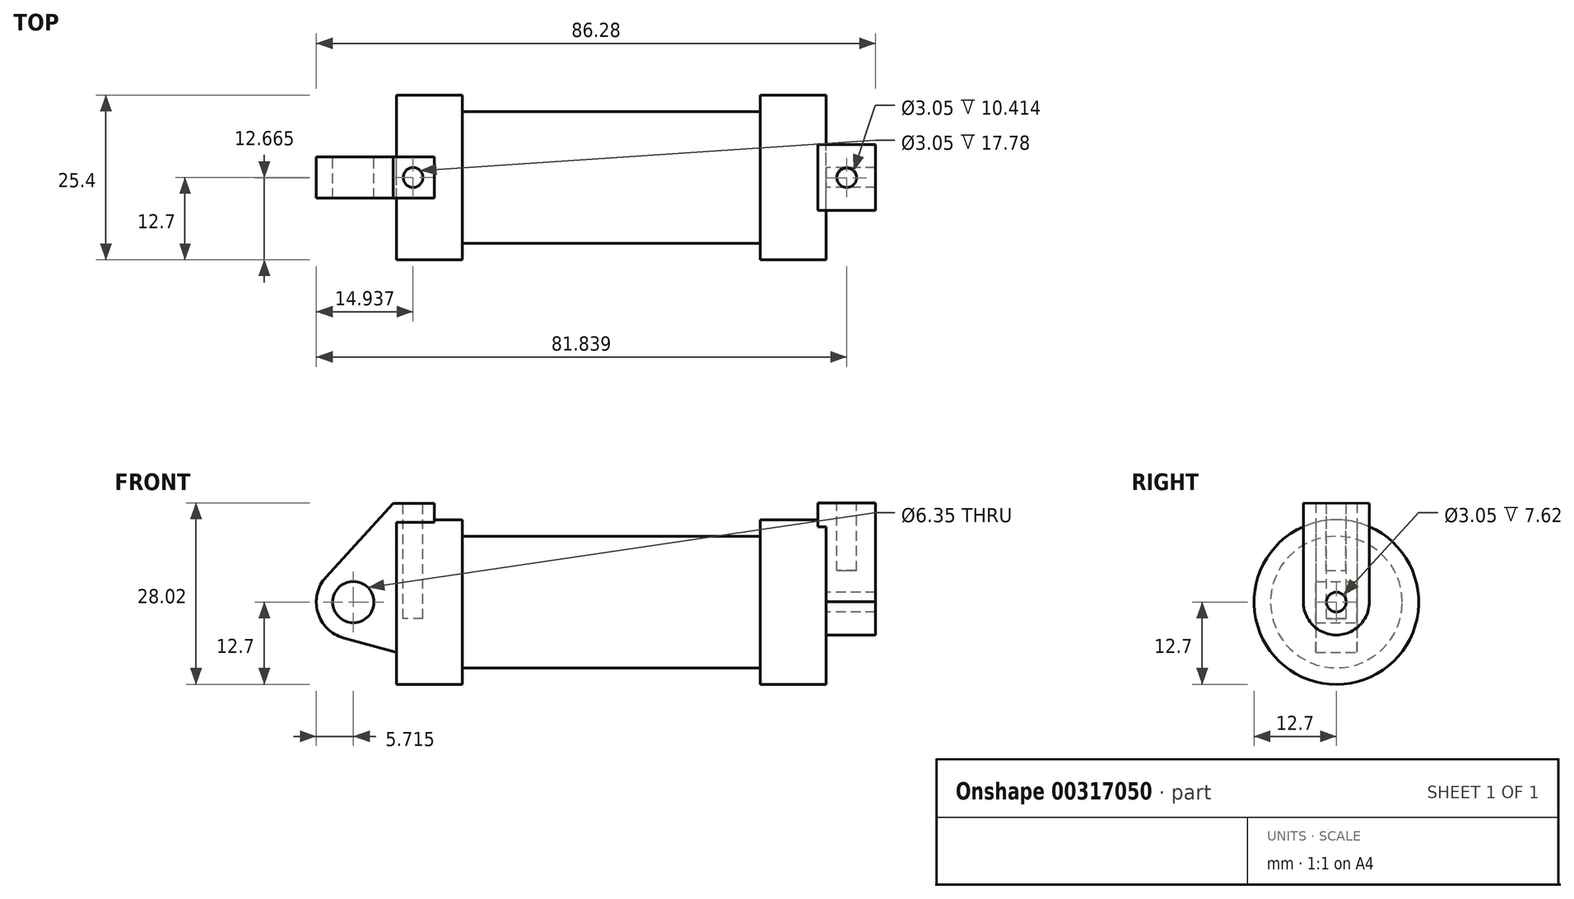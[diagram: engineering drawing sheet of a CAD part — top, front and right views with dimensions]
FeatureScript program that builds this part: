
annotation { "Feature Type Name" : "Feature", "Feature Type Description" : "" }
export const myFeature = defineFeature(function(context is Context, id is Id, definition is map)
    precondition{}
    {
        {
            var Q0;
            Q0=qCreatedBy(makeId("Front.planeOp"),FACE);
            var sketch = newSketch(context, id + "F0", { "sketchPlane" : qUnion([Q0])});
            skLineSegment(sketch, "E0", {"start": v(0, 0) * mm, "end": v(0, 12.7) * mm});
            skLineSegment(sketch, "E1", {"start": v(0, 12.7) * mm, "end": v(10.16, 12.7) * mm});
            skLineSegment(sketch, "E2", {"start": v(10.16, 12.7) * mm, "end": v(10.16, 10.16) * mm});
            skLineSegment(sketch, "E3", {"start": v(10.16, 10.16) * mm, "end": v(56.13, 10.16) * mm});
            skLineSegment(sketch, "E4", {"start": v(56.13, 10.16) * mm, "end": v(56.13, 12.7) * mm});
            skLineSegment(sketch, "E5", {"start": v(56.13, 12.7) * mm, "end": v(66.3, 12.7) * mm});
            skLineSegment(sketch, "E6", {"start": v(66.3, 12.7) * mm, "end": v(66.3, 0) * mm});
            skLineSegment(sketch, "E7", {"start": v(66.3, 0) * mm, "end": v(0, 0) * mm});
            skLineSegment(sketch, "E8", {"start": v(5.84, 15.24) * mm, "end": v(-0.5, 15.24) * mm});
            skLineSegment(sketch, "E9", {"start": v(-0.5, 15.24) * mm, "end": v(-10.88, 3.85) * mm});
            skLineSegment(sketch, "E10", {"start": v(0, 0) * mm, "end": v(-6.65, 0) * mm});
            skCircle(sketch, "E11", {"center": v(-6.65, 0) * mm, "radius": 5.72 * mm});
            skCircle(sketch, "E12", {"center": v(-6.65, 0) * mm, "radius": 3.18 * mm});
            skLineSegment(sketch, "E13", {"start": v(5.84, 15.24) * mm, "end": v(5.84, -9.4) * mm});
            skLineSegment(sketch, "E14", {"start": v(5.84, -9.4) * mm, "end": v(-8.18, -5.5) * mm});
            skSolve(sketch);
        }
        {
            var Q0;
            {var subQ0=sQuery(id+"F0.wireOp",EDGE,"E2");Q0=makeQuery(id+"F0.imprint","IMPRINT",FACE,{"disambiguationData":[TD([[makeQuery(id+"F0.imprint","IMPRINT",EDGE,{"derivedFrom":subQ0}),-1.0]])]});}
            var Q1;
            {var subQ0=sQuery(id+"F0.wireOp",EDGE,"E0");Q1=makeQuery(id+"F0.imprint","IMPRINT",FACE,{"disambiguationData":[TD([[makeQuery(id+"F0.imprint","IMPRINT",EDGE,{"derivedFrom":subQ0}),-1.0]])]});}
            var Q2;
            Q2=sQuery(id+"F0.wireOp",EDGE,"E7");
            revolve(context, id + "F1", {"entities" : qUnion([Q0, Q1]), "axis" : qUnion([Q2]), "revolveType" : RevolveType.FULL});
        }
        {
            var Q0;
            {var subQ1=sQuery(id+"F0.wireOp",EDGE,"E0");Q0=makeQuery(id+"F0.imprint","IMPRINT",FACE,{"disambiguationData":[TD([[makeQuery(id+"F0.imprint","IMPRINT",EDGE,{"derivedFrom":subQ1}),1.0]])]});}
            var Q1;
            {var subQ5=sQuery(id+"F0.wireOp",EDGE,"E12");Q1=makeQuery(id+"F0.imprint","IMPRINT",FACE,{"disambiguationData":[TD([[makeQuery(id+"F0.imprint","IMPRINT",EDGE,{"derivedFrom":subQ5}),-1.0]])]});}
            var Q2;
            {var subQ0=sQuery(id+"F0.wireOp",EDGE,"E14");Q2=makeQuery(id+"F0.imprint","IMPRINT",FACE,{"disambiguationData":[TD([[makeQuery(id+"F0.imprint","IMPRINT",EDGE,{"derivedFrom":subQ0}),-1.0]])]});}
            var Q3;
            {var subQ0=sQuery(id+"F0.wireOp",EDGE,"E0");Q3=makeQuery(id+"F0.imprint","IMPRINT",FACE,{"disambiguationData":[TD([[makeQuery(id+"F0.imprint","IMPRINT",EDGE,{"derivedFrom":subQ0}),-1.0]])]});}
            extrude(context, id + "F2", {"entities" : qUnion([Q0, Q1, Q2, Q3]), "operationType" : NewBodyOperationType.ADD, "depth" : 3.17 * mm});
        }
        {
            var Q0;
            Q0=makeQuery(id+"F2.opExtrude","CAP_FACE",FACE,{"disambiguationData":[OSD([sQuery(id+"F0.wireOp",EDGE,"E8"),sQuery(id+"F0.wireOp",EDGE,"E9"),sQuery(id+"F0.wireOp",EDGE,"E11"),sQuery(id+"F0.wireOp",EDGE,"E12"),sQuery(id+"F0.wireOp",EDGE,"E13"),sQuery(id+"F0.wireOp",EDGE,"E14")])],"isStart":false});
            extrude(context, id + "F3", {"entities" : qUnion([Q0]), "operationType" : NewBodyOperationType.ADD, "oppositeDirection" : true, "depth" : 6.35 * mm});
        }
        {
            var Q0;
            Q0=makeQuery(id+"F1.opRevolve","SWEPT_FACE",FACE,{"disambiguationData":[OSD([sQuery(id+"F0.wireOp",EDGE,"E6")])]});
            var sketch = newSketch(context, id + "F4", { "sketchPlane" : qUnion([Q0])});
            skCircle(sketch, "E15", {"center": v(0, 0) * mm, "radius": 5.08 * mm});
            skCircle(sketch, "E16", {"center": v(0, 0) * mm, "radius": 1.52 * mm});
            skLineSegment(sketch, "E17", {"start": v(-5.08, 0.08) * mm, "end": v(-5.08, 15.32) * mm});
            skLineSegment(sketch, "E18", {"start": v(5.08, 0) * mm, "end": v(5.08, 15.25) * mm});
            skLineSegment(sketch, "E19", {"start": v(-5.08, 15.32) * mm, "end": v(5.08, 15.25) * mm});
            skSolve(sketch);
        }
        {
            var Q0;
            Q0=makeQuery(id+"F4.imprint","IMPRINT",FACE,{"disambiguationData":[TD([[makeQuery(id+"F4.imprint","IMPRINT",EDGE,{"derivedFrom":sQuery(id+"F4.wireOp",EDGE,"E16")}),-1.0]])]});
            var Q1;
            {var subQ0=sQuery(id+"F4.wireOp",EDGE,"E17");var subQ1=sQuery(id+"F4.wireOp",EDGE,"E15");var subQ2=makeQuery(id+"F4.imprint","INTERSECT",VERTEX,{"derivedFrom":[subQ1,subQ0]});Q1=makeQuery(id+"F4.imprint","IMPRINT",FACE,{"disambiguationData":[TD([[makeQuery(id+"F4.imprint","IMPRINT",EDGE,{"disambiguationData":[TD([[subQ2,1.0]])],"derivedFrom":subQ1}),-1.0]])]});}
            var Q2;
            {var subQ0=sQuery(id+"F4.wireOp",EDGE,"E19");Q2=makeQuery(id+"F4.imprint","IMPRINT",FACE,{"disambiguationData":[TD([[makeQuery(id+"F4.imprint","IMPRINT",EDGE,{"derivedFrom":subQ0}),-1.0]])]});}
            extrude(context, id + "F5", {"entities" : qUnion([Q0, Q1, Q2]), "operationType" : NewBodyOperationType.ADD, "depth" : 7.62 * mm});
        }
        {
            var Q0;
            Q0=makeQuery(id+"F5.opExtrude","CAP_FACE",FACE,{"disambiguationData":[OSD([sQuery(id+"F4.wireOp",EDGE,"E15"),sQuery(id+"F4.wireOp",EDGE,"E16"),sQuery(id+"F4.wireOp",EDGE,"E17"),sQuery(id+"F4.wireOp",EDGE,"E18"),sQuery(id+"F4.wireOp",EDGE,"E19")])],"isStart":true});
            extrude(context, id + "F6", {"entities" : qUnion([Q0]), "operationType" : NewBodyOperationType.ADD, "depth" : 1.27 * mm});
        }
        {
            var Q0;
            {var subQ0=sQuery(id+"F0.wireOp",EDGE,"E8");Q0=makeQuery(id+"F3.boolean.opBoolean","MERGE",FACE,{"derivedFrom":[makeQuery(id+"F2.opExtrude","SWEPT_FACE",FACE,{"disambiguationData":[OSD([subQ0])]}),makeQuery(id+"F3.opExtrude","SWEPT_FACE",FACE,{"disambiguationData":[OSD([subQ0])]})]});}
            var sketch = newSketch(context, id + "F7", { "sketchPlane" : qUnion([Q0])});
            skCircle(sketch, "E20", {"center": v(2.57, 0) * mm, "radius": 1.52 * mm});
            skCircle(sketch, "E21", {"center": v(69.47, -0.16) * mm, "radius": 1.52 * mm});
            skSolve(sketch);
        }
        {
            var Q0;
            {var subQ0=sQuery(id+"F4.wireOp",EDGE,"E19");Q0=makeQuery(id+"F6.boolean.opBoolean","MERGE",FACE,{"derivedFrom":[makeQuery(id+"F5.opExtrude","SWEPT_FACE",FACE,{"disambiguationData":[OSD([subQ0])]}),makeQuery(id+"F6.opExtrude","SWEPT_FACE",FACE,{"disambiguationData":[OSD([subQ0])]})]});}
            var sketch = newSketch(context, id + "F8", { "sketchPlane" : qUnion([Q0])});
            skLineSegment(sketch, "E22", {"start": v(65.02, 4.98) * mm, "end": v(73.91, -5.18) * mm, "construction": true});
            skLineSegment(sketch, "E23", {"start": v(65.02, -5.18) * mm, "end": v(73.91, 4.98) * mm, "construction": true});
            skCircle(sketch, "E24", {"center": v(69.47, -0.1) * mm, "radius": 1.52 * mm});
            skSolve(sketch);
        }
        {
            var Q0;
            Q0=makeQuery(id+"F8.imprint","IMPRINT",FACE,{"disambiguationData":[TD([[makeQuery(id+"F8.imprint","IMPRINT",EDGE,{"derivedFrom":sQuery(id+"F8.wireOp",EDGE,"E24")}),1.0]])]});
            extrude(context, id + "F9", {"entities" : qUnion([Q0]), "operationType" : NewBodyOperationType.REMOVE, "oppositeDirection" : true, "depth" : 10.4 * mm});
        }
        {
            var Q0;
            Q0=makeQuery(id+"F7.imprint","IMPRINT",FACE,{"disambiguationData":[TD([[makeQuery(id+"F7.imprint","IMPRINT",EDGE,{"derivedFrom":sQuery(id+"F7.wireOp",EDGE,"E20")}),1.0]])]});
            extrude(context, id + "F10", {"entities" : qUnion([Q0]), "operationType" : NewBodyOperationType.REMOVE, "oppositeDirection" : true, "depth" : 17.78 * mm});
        }
    });
